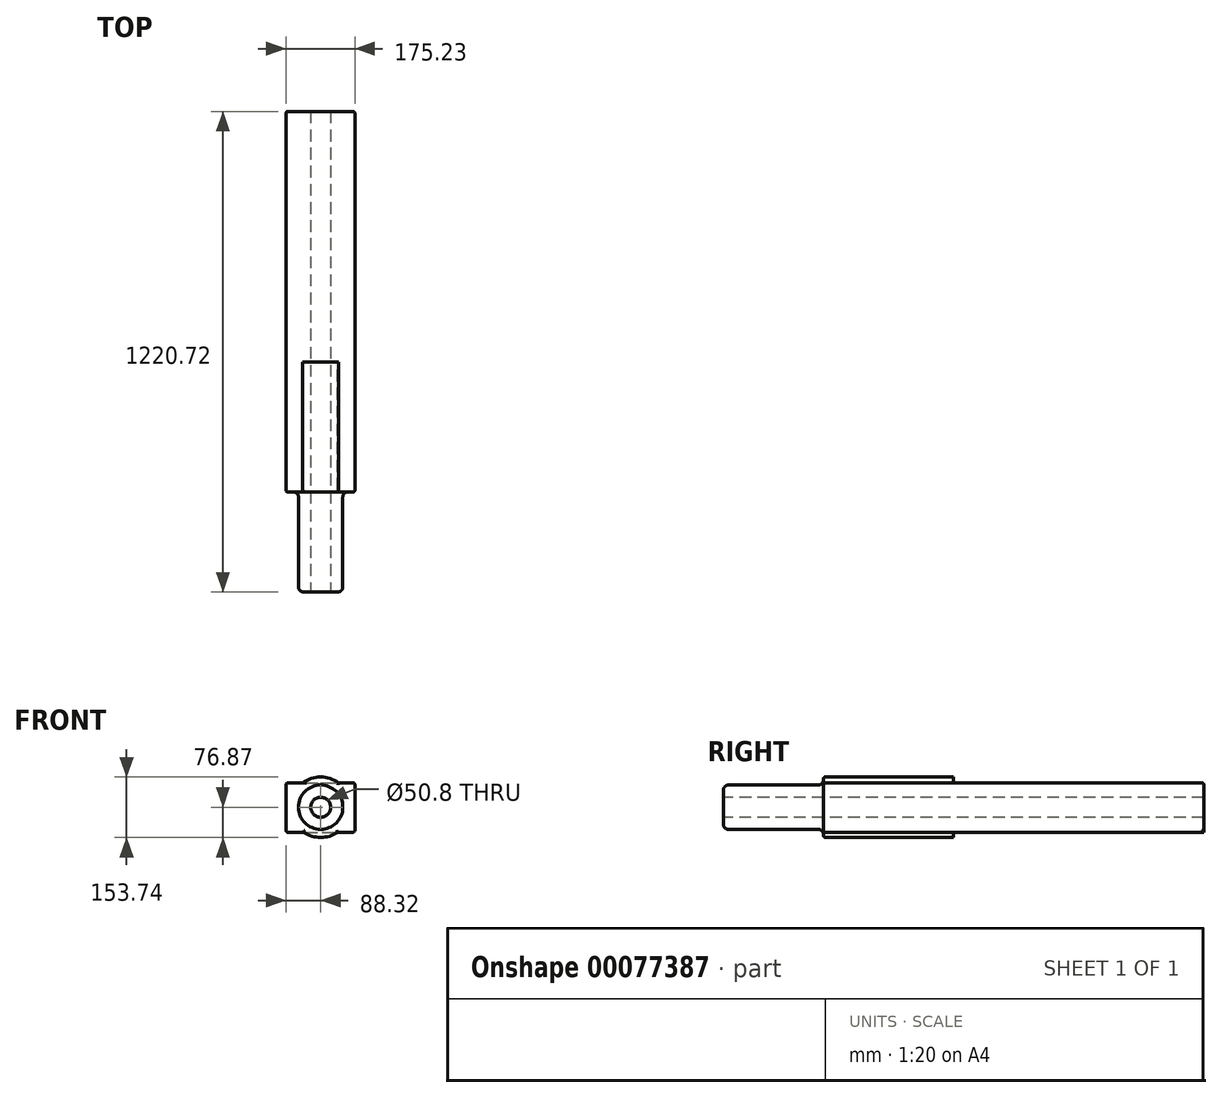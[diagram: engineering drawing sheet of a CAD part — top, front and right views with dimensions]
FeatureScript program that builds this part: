
annotation { "Feature Type Name" : "Feature", "Feature Type Description" : "" }
export const myFeature = defineFeature(function(context is Context, id is Id, definition is map)
    precondition{}
    {
        {
            var Q0;
            Q0=qCreatedBy(makeId("Front.planeOp"),FACE);
            var sketch = newSketch(context, id + "F0", { "sketchPlane" : qUnion([Q0])});
            skCircle(sketch, "E0", {"center": v(0, 0) * mm, "radius": 76.87 * mm});
            skSolve(sketch);
        }
        {
            var Q0;
            Q0=makeQuery(id+"F0.imprint","IMPRINT",FACE,{"disambiguationData":[TD([[makeQuery(id+"F0.imprint","IMPRINT",EDGE,{"derivedFrom":sQuery(id+"F0.wireOp",EDGE,"E0")}),1.0]])]});
            extrude(context, id + "F1", {"entities" : qUnion([Q0]), "depth" : 254 * mm});
        }
        {
            var Q0;
            Q0=makeQuery(id+"F1.opExtrude","CAP_FACE",FACE,{"disambiguationData":[OSD([sQuery(id+"F0.wireOp",EDGE,"E0")])],"isStart":false});
            var sketch = newSketch(context, id + "F2", { "sketchPlane" : qUnion([Q0])});
            skLineSegment(sketch, "E1.bottom", {"start": v(-88.32, 61.88) * mm, "end": v(86.91, 61.88) * mm});
            skLineSegment(sketch, "E1.top", {"start": v(-88.32, -63.72) * mm, "end": v(86.91, -63.72) * mm});
            skLineSegment(sketch, "E1.left", {"start": v(-88.32, 61.88) * mm, "end": v(-88.32, -63.72) * mm});
            skLineSegment(sketch, "E1.right", {"start": v(86.91, 61.88) * mm, "end": v(86.91, -63.72) * mm});
            skSolve(sketch);
        }
        {
            var Q0;
            Q0 = qSketchRegion(id + "F2", true);
            var Q1;
            {var subQ0=sQuery(id+"F2.wireOp",EDGE,"E1.bottom");var subQ1=makeQuery(id+"F1.opExtrude","CAP_EDGE",EDGE,{"disambiguationData":[OSD([sQuery(id+"F0.wireOp",EDGE,"E0")])],"isStart":false});var subQ2=makeQuery(id+"F2.imprint","INTERSECT",VERTEX,{"disambiguationData":[OD(0.0)],"derivedFrom":[subQ1,subQ0]});Q1=makeQuery(id+"F2.imprint","IMPRINT",FACE,{"disambiguationData":[TD([[makeQuery(id+"F2.imprint","IMPRINT",EDGE,{"disambiguationData":[TD([[subQ2,-1.0]])],"derivedFrom":subQ0}),-1.0]])]});}
            extrude(context, id + "F3", {"entities" : qUnion([Q0, Q1]), "operationType" : NewBodyOperationType.ADD, "oppositeDirection" : true, "depth" : 890.52 * mm});
        }
        {
            var Q0;
            Q0=makeQuery(id+"F3.boolean.opBoolean","MERGE",FACE,{"derivedFrom":[makeQuery(id+"F1.opExtrude","CAP_FACE",FACE,{"disambiguationData":[OSD([sQuery(id+"F0.wireOp",EDGE,"E0")])],"isStart":false}),makeQuery(id+"F3.opExtrude","CAP_FACE",FACE,{"disambiguationData":[OSD([sQuery(id+"F2.wireOp",EDGE,"E1.bottom"),sQuery(id+"F2.wireOp",EDGE,"E1.top"),sQuery(id+"F2.wireOp",EDGE,"E1.left"),sQuery(id+"F2.wireOp",EDGE,"E1.right")])],"isStart":true})]});
            var sketch = newSketch(context, id + "F4", { "sketchPlane" : qUnion([Q0])});
            skCircle(sketch, "E2", {"center": v(0, 0) * mm, "radius": 58.92 * mm});
            skSolve(sketch);
        }
        {
            var Q0;
            Q0=makeQuery(id+"F4.imprint","IMPRINT",FACE,{"disambiguationData":[TD([[makeQuery(id+"F4.imprint","IMPRINT",EDGE,{"derivedFrom":sQuery(id+"F4.wireOp",EDGE,"E2")}),1.0]])]});
            var Q1;
            Q1=makeQuery(id+"F3.boolean.opBoolean","MERGE",FACE,{"derivedFrom":[makeQuery(id+"F1.opExtrude","CAP_FACE",FACE,{"disambiguationData":[OSD([sQuery(id+"F0.wireOp",EDGE,"E0")])],"isStart":false}),makeQuery(id+"F3.opExtrude","CAP_FACE",FACE,{"disambiguationData":[OSD([sQuery(id+"F2.wireOp",EDGE,"E1.bottom"),sQuery(id+"F2.wireOp",EDGE,"E1.top"),sQuery(id+"F2.wireOp",EDGE,"E1.left"),sQuery(id+"F2.wireOp",EDGE,"E1.right")])],"isStart":true})]});
            var Q2;
            Q2=makeQuery(id+"F3.opExtrude","CAP_FACE",FACE,{"disambiguationData":[OSD([sQuery(id+"F2.wireOp",EDGE,"E1.bottom"),sQuery(id+"F2.wireOp",EDGE,"E1.top"),sQuery(id+"F2.wireOp",EDGE,"E1.left"),sQuery(id+"F2.wireOp",EDGE,"E1.right")])],"isStart":false});
            extrude(context, id + "F5", {"entities" : qUnion([Q0, Q1, Q2]), "operationType" : NewBodyOperationType.ADD, "depth" : 76.2 * mm});
        }
        {
            var Q0;
            Q0=makeQuery(id+"F5.opExtrude","CAP_FACE",FACE,{"disambiguationData":[OSD([sQuery(id+"F0.wireOp",EDGE,"E0"),sQuery(id+"F2.wireOp",EDGE,"E1.bottom"),sQuery(id+"F2.wireOp",EDGE,"E1.top"),sQuery(id+"F2.wireOp",EDGE,"E1.left"),sQuery(id+"F2.wireOp",EDGE,"E1.right")])],"isStart":false});
            var sketch = newSketch(context, id + "F6", { "sketchPlane" : qUnion([Q0])});
            skCircle(sketch, "E3", {"center": v(0, 0) * mm, "radius": 56.32 * mm});
            skSolve(sketch);
        }
        {
            var Q0;
            Q0=makeQuery(id+"F6.imprint","IMPRINT",FACE,{"disambiguationData":[TD([[makeQuery(id+"F6.imprint","IMPRINT",EDGE,{"derivedFrom":sQuery(id+"F6.wireOp",EDGE,"E3")}),1.0]])]});
            extrude(context, id + "F7", {"entities" : qUnion([Q0]), "operationType" : NewBodyOperationType.ADD, "depth" : 254 * mm, "hasSecondDirection" : true, "secondDirectionOppositeDirection" : true, "secondDirectionDepth" : 25.4 * mm});
        }
        {
            var Q0;
            Q0=makeQuery(id+"F7.boolean.opBoolean","INTERSECT",EDGE,{"derivedFrom":[makeQuery(id+"F5.opExtrude","CAP_FACE",FACE,{"disambiguationData":[OSD([sQuery(id+"F0.wireOp",EDGE,"E0"),sQuery(id+"F2.wireOp",EDGE,"E1.bottom"),sQuery(id+"F2.wireOp",EDGE,"E1.top"),sQuery(id+"F2.wireOp",EDGE,"E1.left"),sQuery(id+"F2.wireOp",EDGE,"E1.right")])],"isStart":false}),makeQuery(id+"F7.opExtrude","SWEPT_FACE",FACE,{"disambiguationData":[OSD([sQuery(id+"F6.wireOp",EDGE,"E3")])]})]});
            fillet(context, id + "F8", {"entities" : qUnion([Q0]), "radius" : 12.7 * mm, "tangentPropagation" : true, "allowEdgeOverflow" : false});
        }
        {
            var Q0;
            Q0=makeQuery(id+"F7.opExtrude","CAP_EDGE",EDGE,{"disambiguationData":[OSD([sQuery(id+"F6.wireOp",EDGE,"E3")])],"isStart":false});
            fillet(context, id + "F9", {"entities" : qUnion([Q0]), "radius" : 12.7 * mm, "tangentPropagation" : true, "allowEdgeOverflow" : false});
        }
        {
            var Q0;
            Q0=makeQuery(id+"F7.opExtrude","CAP_FACE",FACE,{"disambiguationData":[OSD([sQuery(id+"F6.wireOp",EDGE,"E3")])],"isStart":false});
            var sketch = newSketch(context, id + "F10", { "sketchPlane" : qUnion([Q0])});
            skPoint(sketch, "E4", {"position": v(0, 0) * mm});
            skSolve(sketch);
        }
        {
            var Q0;
            Q0=sQuery(id+"F10.wireOp",VERTEX,"E4");
            var Q1;
            Q1=makeQuery(id+"F1.opExtrude","SWEPT_BODY",BODY,{"disambiguationData":[OSD([sQuery(id+"F0.wireOp",EDGE,"E0")])]});
            hole(context, id + "F11", {"style" : HoleStyle.SIMPLE, "endStyle" : HoleEndStyle.THROUGH, "holeDiameter" : 50.8 * mm, "locations" : qUnion([Q0]), "scope" : qUnion([Q1]), "isTappedThrough" : true});
        }
        {
            var Q0;
            {var subQ0=sQuery(id+"F2.wireOp",EDGE,"E1.right");var subQ1=sQuery(id+"F2.wireOp",EDGE,"E1.bottom");Q0=makeQuery(id+"F5.boolean.opBoolean","MERGE",EDGE,{"derivedFrom":[makeQuery(id+"F3.opExtrude","SWEPT_EDGE",EDGE,{"disambiguationData":[OSD([subQ1,subQ0])]}),makeQuery(id+"F5.opExtrude","SWEPT_EDGE",EDGE,{"disambiguationData":[OSD([subQ1,subQ0]),TDD([makeQuery(id+"F3.opExtrude","CAP_VERTEX",VERTEX,{"disambiguationData":[OSD([subQ1,subQ0])],"isStart":true})])]})]});}
            var Q1;
            {var subQ0=sQuery(id+"F2.wireOp",EDGE,"E1.left");var subQ1=sQuery(id+"F2.wireOp",EDGE,"E1.bottom");Q1=makeQuery(id+"F5.boolean.opBoolean","MERGE",EDGE,{"derivedFrom":[makeQuery(id+"F3.opExtrude","SWEPT_EDGE",EDGE,{"disambiguationData":[OSD([subQ1,subQ0])]}),makeQuery(id+"F5.opExtrude","SWEPT_EDGE",EDGE,{"disambiguationData":[OSD([subQ1,subQ0]),TDD([makeQuery(id+"F3.opExtrude","CAP_VERTEX",VERTEX,{"disambiguationData":[OSD([subQ1,subQ0])],"isStart":true})])]})]});}
            var Q2;
            {var subQ0=sQuery(id+"F2.wireOp",EDGE,"E1.right");var subQ1=sQuery(id+"F2.wireOp",EDGE,"E1.top");Q2=makeQuery(id+"F5.boolean.opBoolean","MERGE",EDGE,{"derivedFrom":[makeQuery(id+"F3.opExtrude","SWEPT_EDGE",EDGE,{"disambiguationData":[OSD([subQ1,subQ0])]}),makeQuery(id+"F5.opExtrude","SWEPT_EDGE",EDGE,{"disambiguationData":[OSD([subQ1,subQ0]),TDD([makeQuery(id+"F3.opExtrude","CAP_VERTEX",VERTEX,{"disambiguationData":[OSD([subQ1,subQ0])],"isStart":true})])]})]});}
            var Q3;
            {var subQ0=sQuery(id+"F2.wireOp",EDGE,"E1.right");Q3=makeQuery(id+"F5.opExtrude","CAP_EDGE",EDGE,{"disambiguationData":[OSD([subQ0]),TDD([makeQuery(id+"F3.opExtrude","CAP_EDGE",EDGE,{"disambiguationData":[OSD([subQ0])],"isStart":true})])],"isStart":false});}
            var Q4;
            {var subQ0=sQuery(id+"F2.wireOp",EDGE,"E1.left");Q4=makeQuery(id+"F5.opExtrude","CAP_EDGE",EDGE,{"disambiguationData":[OSD([subQ0]),TDD([makeQuery(id+"F3.opExtrude","CAP_EDGE",EDGE,{"disambiguationData":[OSD([subQ0])],"isStart":true})])],"isStart":false});}
            var Q5;
            Q5=makeQuery(id+"F3.opExtrude","CAP_EDGE",EDGE,{"disambiguationData":[OSD([sQuery(id+"F2.wireOp",EDGE,"E1.right")])],"isStart":false});
            var Q6;
            Q6=makeQuery(id+"F3.opExtrude","CAP_EDGE",EDGE,{"disambiguationData":[OSD([sQuery(id+"F2.wireOp",EDGE,"E1.bottom")])],"isStart":false});
            var Q7;
            {var subQ0=sQuery(id+"F2.wireOp",EDGE,"E1.left");var subQ1=sQuery(id+"F2.wireOp",EDGE,"E1.top");Q7=makeQuery(id+"F5.boolean.opBoolean","MERGE",EDGE,{"derivedFrom":[makeQuery(id+"F3.opExtrude","SWEPT_EDGE",EDGE,{"disambiguationData":[OSD([subQ1,subQ0])]}),makeQuery(id+"F5.opExtrude","SWEPT_EDGE",EDGE,{"disambiguationData":[OSD([subQ1,subQ0]),TDD([makeQuery(id+"F3.opExtrude","CAP_VERTEX",VERTEX,{"disambiguationData":[OSD([subQ1,subQ0])],"isStart":true})])]})]});}
            var Q8;
            {var subQ1=sQuery(id+"F2.wireOp",EDGE,"E1.top");var subQ2=sQuery(id+"F2.wireOp",EDGE,"E1.right");Q8=makeQuery(id+"F5.opExtrude","CAP_EDGE",EDGE,{"disambiguationData":[OSD([subQ1]),TDD([makeQuery(id+"F3.boolean.opBoolean","SPLIT",EDGE,{"disambiguationData":[TD([makeQuery(id+"F3.opExtrude","SWEPT_FACE",FACE,{"disambiguationData":[OSD([subQ2])]})])],"derivedFrom":makeQuery(id+"F3.opExtrude","CAP_EDGE",EDGE,{"disambiguationData":[OSD([subQ1])],"isStart":true})})])],"isStart":false});}
            var Q9;
            {var subQ0=sQuery(id+"F0.wireOp",EDGE,"E0");var subQ1=sQuery(id+"F2.wireOp",EDGE,"E1.top");Q9=makeQuery(id+"F5.opExtrude","CAP_EDGE",EDGE,{"disambiguationData":[OSD([subQ0]),TDD([makeQuery(id+"F3.boolean.opBoolean","SPLIT",EDGE,{"disambiguationData":[TD([makeQuery(id+"F3.opExtrude","SWEPT_FACE",FACE,{"disambiguationData":[OSD([subQ1])]})])],"derivedFrom":makeQuery(id+"F1.opExtrude","CAP_EDGE",EDGE,{"disambiguationData":[OSD([subQ0])],"isStart":false})})])],"isStart":false});}
            var Q10;
            {var subQ1=sQuery(id+"F2.wireOp",EDGE,"E1.top");var subQ2=sQuery(id+"F2.wireOp",EDGE,"E1.left");Q10=makeQuery(id+"F5.opExtrude","CAP_EDGE",EDGE,{"disambiguationData":[OSD([subQ1]),TDD([makeQuery(id+"F3.boolean.opBoolean","SPLIT",EDGE,{"disambiguationData":[TD([makeQuery(id+"F3.opExtrude","SWEPT_FACE",FACE,{"disambiguationData":[OSD([subQ2])]})])],"derivedFrom":makeQuery(id+"F3.opExtrude","CAP_EDGE",EDGE,{"disambiguationData":[OSD([subQ1])],"isStart":true})})])],"isStart":false});}
            var Q11;
            {var subQ1=sQuery(id+"F2.wireOp",EDGE,"E1.right");var subQ2=sQuery(id+"F2.wireOp",EDGE,"E1.bottom");Q11=makeQuery(id+"F5.opExtrude","CAP_EDGE",EDGE,{"disambiguationData":[OSD([subQ2]),TDD([makeQuery(id+"F3.boolean.opBoolean","SPLIT",EDGE,{"disambiguationData":[TD([makeQuery(id+"F3.opExtrude","SWEPT_FACE",FACE,{"disambiguationData":[OSD([subQ1])]})])],"derivedFrom":makeQuery(id+"F3.opExtrude","CAP_EDGE",EDGE,{"disambiguationData":[OSD([subQ2])],"isStart":true})})])],"isStart":false});}
            var Q12;
            {var subQ0=sQuery(id+"F0.wireOp",EDGE,"E0");var subQ1=sQuery(id+"F2.wireOp",EDGE,"E1.bottom");Q12=makeQuery(id+"F5.opExtrude","CAP_EDGE",EDGE,{"disambiguationData":[OSD([subQ0]),TDD([makeQuery(id+"F3.boolean.opBoolean","SPLIT",EDGE,{"disambiguationData":[TD([makeQuery(id+"F3.opExtrude","SWEPT_FACE",FACE,{"disambiguationData":[OSD([subQ1])]})])],"derivedFrom":makeQuery(id+"F1.opExtrude","CAP_EDGE",EDGE,{"disambiguationData":[OSD([subQ0])],"isStart":false})})])],"isStart":false});}
            var Q13;
            {var subQ0=sQuery(id+"F2.wireOp",EDGE,"E1.left");Q13=makeQuery(id+"F5.boolean.opBoolean","MERGE",FACE,{"derivedFrom":[makeQuery(id+"F3.opExtrude","SWEPT_FACE",FACE,{"disambiguationData":[OSD([subQ0])]}),makeQuery(id+"F5.opExtrude","SWEPT_FACE",FACE,{"disambiguationData":[OSD([subQ0]),TDD([makeQuery(id+"F3.opExtrude","CAP_EDGE",EDGE,{"disambiguationData":[OSD([subQ0])],"isStart":true})])]})]});}
            fillet(context, id + "F12", {"entities" : qUnion([Q0, Q1, Q2, Q3, Q4, Q5, Q6, Q7, Q8, Q9, Q10, Q11, Q12, Q13]), "radius" : 5.08 * mm, "tangentPropagation" : true, "allowEdgeOverflow" : false});
        }
    });
